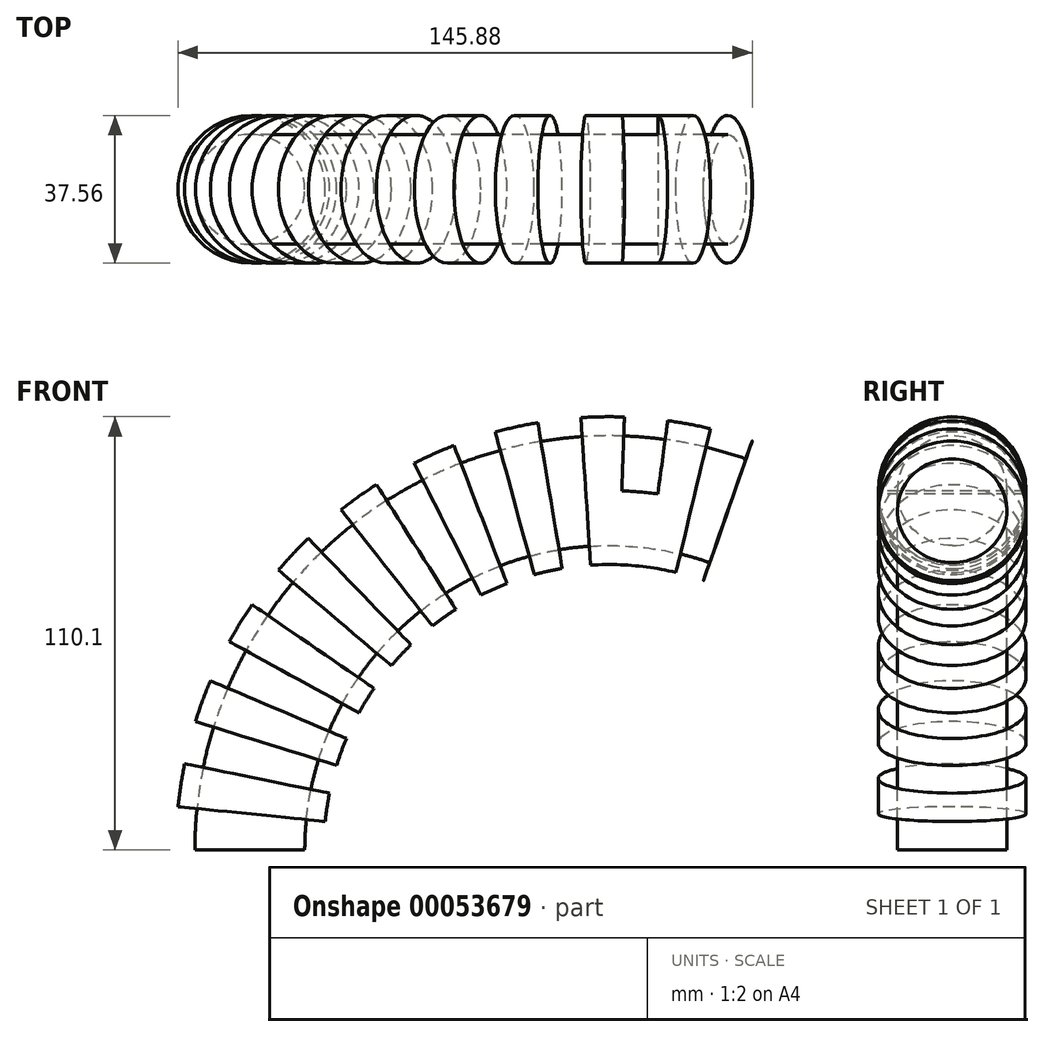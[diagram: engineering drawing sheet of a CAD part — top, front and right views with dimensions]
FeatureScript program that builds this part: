
annotation { "Feature Type Name" : "Feature", "Feature Type Description" : "" }
export const myFeature = defineFeature(function(context is Context, id is Id, definition is map)
    precondition{}
    {
        {
            var Q0;
            Q0=qCreatedBy(makeId("Top.planeOp"),FACE);
            var sketch = newSketch(context, id + "F0", { "sketchPlane" : qUnion([Q0])});
            skCircle(sketch, "E0", {"center": v(0, 0) * mm, "radius": 13.96 * mm});
            skCircle(sketch, "E1", {"center": v(0, 0) * mm, "radius": 18.78 * mm});
            skSolve(sketch);
        }
        {
            var Q0;
            Q0=qCreatedBy(makeId("Front.planeOp"),FACE);
            var sketch = newSketch(context, id + "F1", { "sketchPlane" : qUnion([Q0])});
            skArc(sketch, "E2", {"start": v(121.45, 86.2) * mm, "mid": v(38.46, 74.47) * mm, "end": v(0, 0) * mm});
            skArc(sketch, "E3", {"start": v(-91.58, 18.42) * mm, "mid": v(-92.28, 9.22) * mm, "end": v(-92.5, 0) * mm});
            skLineSegment(sketch, "E4", {"start": v(52.75, 0) * mm, "end": v(-92.5, 0) * mm});
            skLineSegment(sketch, "E5.1.0", {"start": v(52.94, 3.86) * mm, "end": v(-91.58, 18.42) * mm});
            skLineSegment(sketch, "E5.2.0", {"start": v(53.52, 7.69) * mm, "end": v(-88.82, 36.65) * mm});
            skLineSegment(sketch, "E5.3.0", {"start": v(91.32, 0) * mm, "end": v(-84.24, 54.5) * mm});
            skLineSegment(sketch, "E5.4.0", {"start": v(55.82, 15.07) * mm, "end": v(-77.9, 71.82) * mm});
            skLineSegment(sketch, "E5.5.0", {"start": v(57.5, 18.55) * mm, "end": v(-69.85, 88.41) * mm});
            skLineSegment(sketch, "E5.6.0", {"start": v(59.53, 21.85) * mm, "end": v(-60.18, 104.12) * mm});
            skLineSegment(sketch, "E5.7.0", {"start": v(61.88, 24.92) * mm, "end": v(-48.99, 118.77) * mm});
            skLineSegment(sketch, "E5.8.0", {"start": v(64.53, 27.75) * mm, "end": v(-36.38, 132.23) * mm});
            skLineSegment(sketch, "E5.9.0", {"start": v(91.32, 0) * mm, "end": v(-22.5, 144.36) * mm});
            skLineSegment(sketch, "E5.10.0", {"start": v(70.6, 32.53) * mm, "end": v(-7.46, 155.03) * mm});
            skLineSegment(sketch, "E5.11.0", {"start": v(73.96, 34.44) * mm, "end": v(8.57, 164.15) * mm});
            skLineSegment(sketch, "E5.12.0", {"start": v(91.32, 0) * mm, "end": v(25.43, 171.61) * mm});
            skLineSegment(sketch, "E5.13.0", {"start": v(81.17, 37.21) * mm, "end": v(42.96, 177.35) * mm});
            skLineSegment(sketch, "E5.14.0", {"start": v(84.95, 38.04) * mm, "end": v(60.97, 181.3) * mm});
            skLineSegment(sketch, "E5.15.0", {"start": v(88.8, 38.5) * mm, "end": v(79.28, 183.43) * mm});
            skLineSegment(sketch, "E5.16.0", {"start": v(92.66, 38.55) * mm, "end": v(97.72, 183.72) * mm});
            skLineSegment(sketch, "E5.17.0", {"start": v(103.63, 90.49) * mm, "end": v(116.1, 182.15) * mm});
            skLineSegment(sketch, "E5.18.0", {"start": v(91.32, 0) * mm, "end": v(134.22, 178.75) * mm});
            skLineSegment(sketch, "E5.19.0", {"start": v(91.32, 0) * mm, "end": v(151.9, 173.56) * mm});
            skLineSegment(sketch, "E5.anchor1", {"start": v(91.32, 0) * mm, "end": v(-92.5, 0) * mm, "construction": true});
            skLineSegment(sketch, "E5.anchor2", {"start": v(91.32, 0) * mm, "end": v(151.9, 173.56) * mm, "construction": true});
            skCircle(sketch, "E6", {"center": v(91.32, 0) * mm, "radius": 38.57 * mm});
            skArc(sketch, "E7.trimOffspring", {"start": v(151.9, 173.56) * mm, "mid": v(143.13, 176.38) * mm, "end": v(134.22, 178.75) * mm});
            skArc(sketch, "E8.trimOffspring", {"start": v(-84.24, 54.5) * mm, "mid": v(-86.75, 45.64) * mm, "end": v(-88.82, 36.65) * mm});
            skArc(sketch, "E9.trimOffspring", {"start": v(-69.85, 88.41) * mm, "mid": v(-74.08, 80.22) * mm, "end": v(-77.9, 71.82) * mm});
            skArc(sketch, "E10.trimOffspring", {"start": v(-48.99, 118.77) * mm, "mid": v(-54.77, 111.58) * mm, "end": v(-60.18, 104.12) * mm});
            skArc(sketch, "E11.trimOffspring", {"start": v(-22.5, 144.36) * mm, "mid": v(-29.6, 138.47) * mm, "end": v(-36.38, 132.23) * mm});
            skArc(sketch, "E12.trimOffspring", {"start": v(8.57, 164.15) * mm, "mid": v(0.44, 159.8) * mm, "end": v(-7.46, 155.03) * mm});
            skArc(sketch, "E13.trimOffspring", {"start": v(42.96, 177.35) * mm, "mid": v(34.12, 174.7) * mm, "end": v(25.43, 171.61) * mm});
            skArc(sketch, "E14.trimOffspring", {"start": v(79.28, 183.43) * mm, "mid": v(70.1, 182.6) * mm, "end": v(60.97, 181.3) * mm});
            skArc(sketch, "E15.trimOffspring", {"start": v(116.1, 182.15) * mm, "mid": v(106.93, 183.17) * mm, "end": v(97.72, 183.72) * mm});
            skSolve(sketch);
        }
        {
            var Q0;
            Q0=makeQuery(id+"F0.imprint","IMPRINT",FACE,{"disambiguationData":[TD([[makeQuery(id+"F0.imprint","IMPRINT",EDGE,{"derivedFrom":sQuery(id+"F0.wireOp",EDGE,"E0")}),1.0]])]});
            var Q1;
            Q1=makeQuery(id+"F0.imprint","IMPRINT",FACE,{"disambiguationData":[TD([[makeQuery(id+"F0.imprint","IMPRINT",EDGE,{"derivedFrom":sQuery(id+"F0.wireOp",EDGE,"E0")}),-1.0]])]});
            var Q2;
            Q2=sQuery(id+"F1.wireOp",EDGE,"E2");
            sweep(context, id + "F2", {"profiles" : qUnion([Q0, Q1]), "path" : qUnion([Q2])});
        }
        {
            var Q0;
            {var subQ5=sQuery(id+"F1.wireOp",EDGE,"E3");Q0=makeQuery(id+"F1.imprint","IMPRINT",FACE,{"disambiguationData":[TD([[makeQuery(id+"F1.imprint","IMPRINT",EDGE,{"derivedFrom":subQ5}),1.0]])]});}
            var Q1;
            {var subQ5=sQuery(id+"F1.wireOp",EDGE,"E8.trimOffspring");Q1=makeQuery(id+"F1.imprint","IMPRINT",FACE,{"disambiguationData":[TD([[makeQuery(id+"F1.imprint","IMPRINT",EDGE,{"derivedFrom":subQ5}),1.0]])]});}
            var Q2;
            {var subQ5=sQuery(id+"F1.wireOp",EDGE,"E9.trimOffspring");Q2=makeQuery(id+"F1.imprint","IMPRINT",FACE,{"disambiguationData":[TD([[makeQuery(id+"F1.imprint","IMPRINT",EDGE,{"derivedFrom":subQ5}),1.0]])]});}
            var Q3;
            {var subQ5=sQuery(id+"F1.wireOp",EDGE,"E10.trimOffspring");Q3=makeQuery(id+"F1.imprint","IMPRINT",FACE,{"disambiguationData":[TD([[makeQuery(id+"F1.imprint","IMPRINT",EDGE,{"derivedFrom":subQ5}),1.0]])]});}
            var Q4;
            {var subQ5=sQuery(id+"F1.wireOp",EDGE,"E11.trimOffspring");Q4=makeQuery(id+"F1.imprint","IMPRINT",FACE,{"disambiguationData":[TD([[makeQuery(id+"F1.imprint","IMPRINT",EDGE,{"derivedFrom":subQ5}),1.0]])]});}
            var Q5;
            {var subQ5=sQuery(id+"F1.wireOp",EDGE,"E12.trimOffspring");Q5=makeQuery(id+"F1.imprint","IMPRINT",FACE,{"disambiguationData":[TD([[makeQuery(id+"F1.imprint","IMPRINT",EDGE,{"derivedFrom":subQ5}),1.0]])]});}
            var Q6;
            {var subQ5=sQuery(id+"F1.wireOp",EDGE,"E13.trimOffspring");Q6=makeQuery(id+"F1.imprint","IMPRINT",FACE,{"disambiguationData":[TD([[makeQuery(id+"F1.imprint","IMPRINT",EDGE,{"derivedFrom":subQ5}),1.0]])]});}
            var Q7;
            {var subQ5=sQuery(id+"F1.wireOp",EDGE,"E14.trimOffspring");Q7=makeQuery(id+"F1.imprint","IMPRINT",FACE,{"disambiguationData":[TD([[makeQuery(id+"F1.imprint","IMPRINT",EDGE,{"derivedFrom":subQ5}),1.0]])]});}
            var Q8;
            {var subQ0=sQuery(id+"F1.wireOp",EDGE,"E5.17.0");Q8=makeQuery(id+"F1.imprint","IMPRINT",FACE,{"disambiguationData":[TD([[makeQuery(id+"F1.imprint","IMPRINT",EDGE,{"derivedFrom":subQ0}),1.0]])]});}
            var Q9;
            {var subQ5=sQuery(id+"F1.wireOp",EDGE,"E7.trimOffspring");Q9=makeQuery(id+"F1.imprint","IMPRINT",FACE,{"disambiguationData":[TD([[makeQuery(id+"F1.imprint","IMPRINT",EDGE,{"derivedFrom":subQ5}),1.0]])]});}
            var Q10;
            {var subQ0=sQuery(id+"F1.wireOp",EDGE,"E5.19.0");var subQ1=sQuery(id+"F1.wireOp",EDGE,"E2");var subQ2=makeQuery(id+"F1.imprint","INTERSECT",VERTEX,{"derivedFrom":[subQ1,subQ0]});Q10=makeQuery(id+"F1.imprint","IMPRINT",FACE,{"disambiguationData":[TD([[makeQuery(id+"F1.imprint","IMPRINT",EDGE,{"disambiguationData":[TD([[subQ2,-1.0]])],"derivedFrom":subQ1}),1.0]])]});}
            var Q11;
            {var subQ0=sQuery(id+"F1.wireOp",EDGE,"E5.15.0");var subQ1=sQuery(id+"F1.wireOp",EDGE,"E2");var subQ2=makeQuery(id+"F1.imprint","INTERSECT",VERTEX,{"derivedFrom":[subQ1,subQ0]});Q11=makeQuery(id+"F1.imprint","IMPRINT",FACE,{"disambiguationData":[TD([[makeQuery(id+"F1.imprint","IMPRINT",EDGE,{"disambiguationData":[TD([[subQ2,-1.0]])],"derivedFrom":subQ1}),1.0]])]});}
            var Q12;
            {var subQ0=sQuery(id+"F1.wireOp",EDGE,"E5.13.0");var subQ1=sQuery(id+"F1.wireOp",EDGE,"E2");var subQ2=makeQuery(id+"F1.imprint","INTERSECT",VERTEX,{"derivedFrom":[subQ1,subQ0]});Q12=makeQuery(id+"F1.imprint","IMPRINT",FACE,{"disambiguationData":[TD([[makeQuery(id+"F1.imprint","IMPRINT",EDGE,{"disambiguationData":[TD([[subQ2,-1.0]])],"derivedFrom":subQ1}),1.0]])]});}
            var Q13;
            {var subQ0=sQuery(id+"F1.wireOp",EDGE,"E5.11.0");var subQ1=sQuery(id+"F1.wireOp",EDGE,"E2");var subQ2=makeQuery(id+"F1.imprint","INTERSECT",VERTEX,{"derivedFrom":[subQ1,subQ0]});Q13=makeQuery(id+"F1.imprint","IMPRINT",FACE,{"disambiguationData":[TD([[makeQuery(id+"F1.imprint","IMPRINT",EDGE,{"disambiguationData":[TD([[subQ2,-1.0]])],"derivedFrom":subQ1}),1.0]])]});}
            var Q14;
            {var subQ0=sQuery(id+"F1.wireOp",EDGE,"E5.9.0");var subQ1=sQuery(id+"F1.wireOp",EDGE,"E2");var subQ2=makeQuery(id+"F1.imprint","INTERSECT",VERTEX,{"derivedFrom":[subQ1,subQ0]});Q14=makeQuery(id+"F1.imprint","IMPRINT",FACE,{"disambiguationData":[TD([[makeQuery(id+"F1.imprint","IMPRINT",EDGE,{"disambiguationData":[TD([[subQ2,-1.0]])],"derivedFrom":subQ1}),1.0]])]});}
            var Q15;
            {var subQ0=sQuery(id+"F1.wireOp",EDGE,"E5.7.0");var subQ1=sQuery(id+"F1.wireOp",EDGE,"E2");var subQ2=makeQuery(id+"F1.imprint","INTERSECT",VERTEX,{"derivedFrom":[subQ1,subQ0]});Q15=makeQuery(id+"F1.imprint","IMPRINT",FACE,{"disambiguationData":[TD([[makeQuery(id+"F1.imprint","IMPRINT",EDGE,{"disambiguationData":[TD([[subQ2,-1.0]])],"derivedFrom":subQ1}),1.0]])]});}
            var Q16;
            {var subQ0=sQuery(id+"F1.wireOp",EDGE,"E5.5.0");var subQ1=sQuery(id+"F1.wireOp",EDGE,"E2");var subQ2=makeQuery(id+"F1.imprint","INTERSECT",VERTEX,{"derivedFrom":[subQ1,subQ0]});Q16=makeQuery(id+"F1.imprint","IMPRINT",FACE,{"disambiguationData":[TD([[makeQuery(id+"F1.imprint","IMPRINT",EDGE,{"disambiguationData":[TD([[subQ2,-1.0]])],"derivedFrom":subQ1}),1.0]])]});}
            var Q17;
            {var subQ0=sQuery(id+"F1.wireOp",EDGE,"E5.3.0");var subQ1=sQuery(id+"F1.wireOp",EDGE,"E2");var subQ2=makeQuery(id+"F1.imprint","INTERSECT",VERTEX,{"derivedFrom":[subQ1,subQ0]});Q17=makeQuery(id+"F1.imprint","IMPRINT",FACE,{"disambiguationData":[TD([[makeQuery(id+"F1.imprint","IMPRINT",EDGE,{"disambiguationData":[TD([[subQ2,-1.0]])],"derivedFrom":subQ1}),1.0]])]});}
            var Q18;
            {var subQ0=sQuery(id+"F1.wireOp",EDGE,"E4");var subQ1=sQuery(id+"F1.wireOp",EDGE,"E2");var subQ2=makeQuery(id+"F1.imprint","INTERSECT",VERTEX,{"derivedFrom":[subQ1,subQ0]});Q18=makeQuery(id+"F1.imprint","IMPRINT",FACE,{"disambiguationData":[TD([[makeQuery(id+"F1.imprint","IMPRINT",EDGE,{"disambiguationData":[TD([[subQ2,1.0]])],"derivedFrom":subQ1}),1.0]])]});}
            extrude(context, id + "F3", {"entities" : qUnion([Q0, Q1, Q2, Q3, Q4, Q5, Q6, Q7, Q8, Q9, Q10, Q11, Q12, Q13, Q14, Q15, Q16, Q17, Q18]), "operationType" : NewBodyOperationType.REMOVE, "endBound" : BoundingType.THROUGH_ALL, "oppositeDirection" : true, "depth" : 25.4 * mm, "hasSecondDirection" : true, "secondDirectionBound" : SecondDirectionBoundingType.THROUGH_ALL, "secondDirectionOppositeDirection" : false, "secondDirectionDepth" : 25.4 * mm});
        }
        {
            var Q0;
            Q0=makeQuery(id+"F0.imprint","IMPRINT",FACE,{"disambiguationData":[TD([[makeQuery(id+"F0.imprint","IMPRINT",EDGE,{"derivedFrom":sQuery(id+"F0.wireOp",EDGE,"E0")}),1.0]])]});
            var Q1;
            Q1=sQuery(id+"F1.wireOp",EDGE,"E2");
            sweep(context, id + "F4", {"profiles" : qUnion([Q0]), "path" : qUnion([Q1])});
        }
    });
